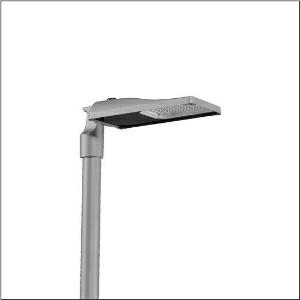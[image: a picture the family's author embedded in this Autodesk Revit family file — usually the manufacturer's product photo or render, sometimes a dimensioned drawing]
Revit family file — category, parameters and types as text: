
# Revit family: streetlight_sl_31_mini___st1_0a_5xh6d31s08ha_c5f6
name_source: partatom
category: Lighting Fixtures
units: mm (PartAtom-declared; Revit-internal decimal feet)

## family parameters
Cut with Voids When Loaded = No
Host = Face
Light Source = No
Part Type = Normal
Room Calculation Point = No
Round Connector Dimension = Use Diameter
Shared = No

## types (1)
- --- (1 x LED, 9230 lm, 68.3 W, 3000K)
    Apparent Load = 68 VA
    CIE Flux Codes = 37 72 97 100 100
    Color Rendering = 70
    Color Temperature = 3000K
    Default Elevation = 1800 mm
    Description = Streetlight SL 31 mini D4i, Desk-Remote mast luminaire for post-top, side-entry; light control with lens of PMMA; light distribution: ST1.0a, direct asymmetric distribution, for standard-compliant lighting for roads and squares; LED: luminous flux: 9.230lm, light colour: 730, colour temperature: 3000K; luminous efficacy: 135,1lm/W; control: pre-setting: logarithmic dimming characteristic, flexible luminous flux parameterisation, time-dependent luminous flux control, constant luminous flux control, power reduction, intelligent temperature release in ECG and LED module, overheat protection; luminaire housing, of diecast aluminium, Siteco® metallic grey (DB 702S), corrosivity category C5 high according to DIN EN ISO 12944; cover of toughened safety glass, transparent, opened without tools; mast flange of diecast aluminium, Siteco® metallic grey (DB 702S), spigot size: 76/60mm, mast flange included unmounted; with cable H07RN-F 2x 1.5mm², cable length: 8,5m, connection cable pre-assembled; mains connection: 220..240V, AC, 50/60Hz; power consumption (at start of service life): 68,3W / (at end of service life): 74,5W / (with reduced operation 50%): 29,5W; protection rating (complete): IP66; insulation class (complete): insulation class II (safety insulation); impact resistance: IK10; certification: CE, ENEC, ENEC+, VDE, UKCA, ZD4i; permissible operating ambient temperature for outdoor applications: -40..+50°C; packaging unit: 1 piece

Light Distribution: ST1.0a
    Height = 76 mm
    Lamp = 1 x LED
    Lamp Light Flux = 9230 lm
    Lamp Power = 68.3 W
    Lamp count = 1
    Length = 547 mm
    Luminous efficacy = 135 lm/W
    Manufacturer = Siteco
    ModVariant = No
    Model = 5XH6D31S08HA
    Number of Poles = 1
    OnlyDefault = Yes
    Power Factor = 1
    Product Name = Streetlight SL 31 mini | ST1.0a
    Product group = mast luminaire | pylon top
    ProductGroupID = 6100
    Protection Class = Protection class II
    Protection Degree = IP 66
    RLX_Detail_Level = 1
    RLX_Emergency_Light_Flux = 0 lm
    RLX_Emergency_Type = 0
    RLX_Emergency_Type_DB = No
    RlxData = <blob elided: 24185 chars, md5=aa4694ec>
    Socket = socket
    Standby Power = 0 W
    System Light Flux = 9230 lm
    System Power = 68 W
    Type Comments = factory setting: luminous flux: 100 % | dim-lin: 254 | 692 mA
    Type Image = l_1300330.jpg
    URL = http://relux.com
    VarID = @adj_019265
    Voltage = 0 V
    Weight = 0.00 kg
    Width = 265 mm

## geometry (parser evidence)
native form markers: Blend x4, Sweep x12
no freeform markers — native parametric forms only
